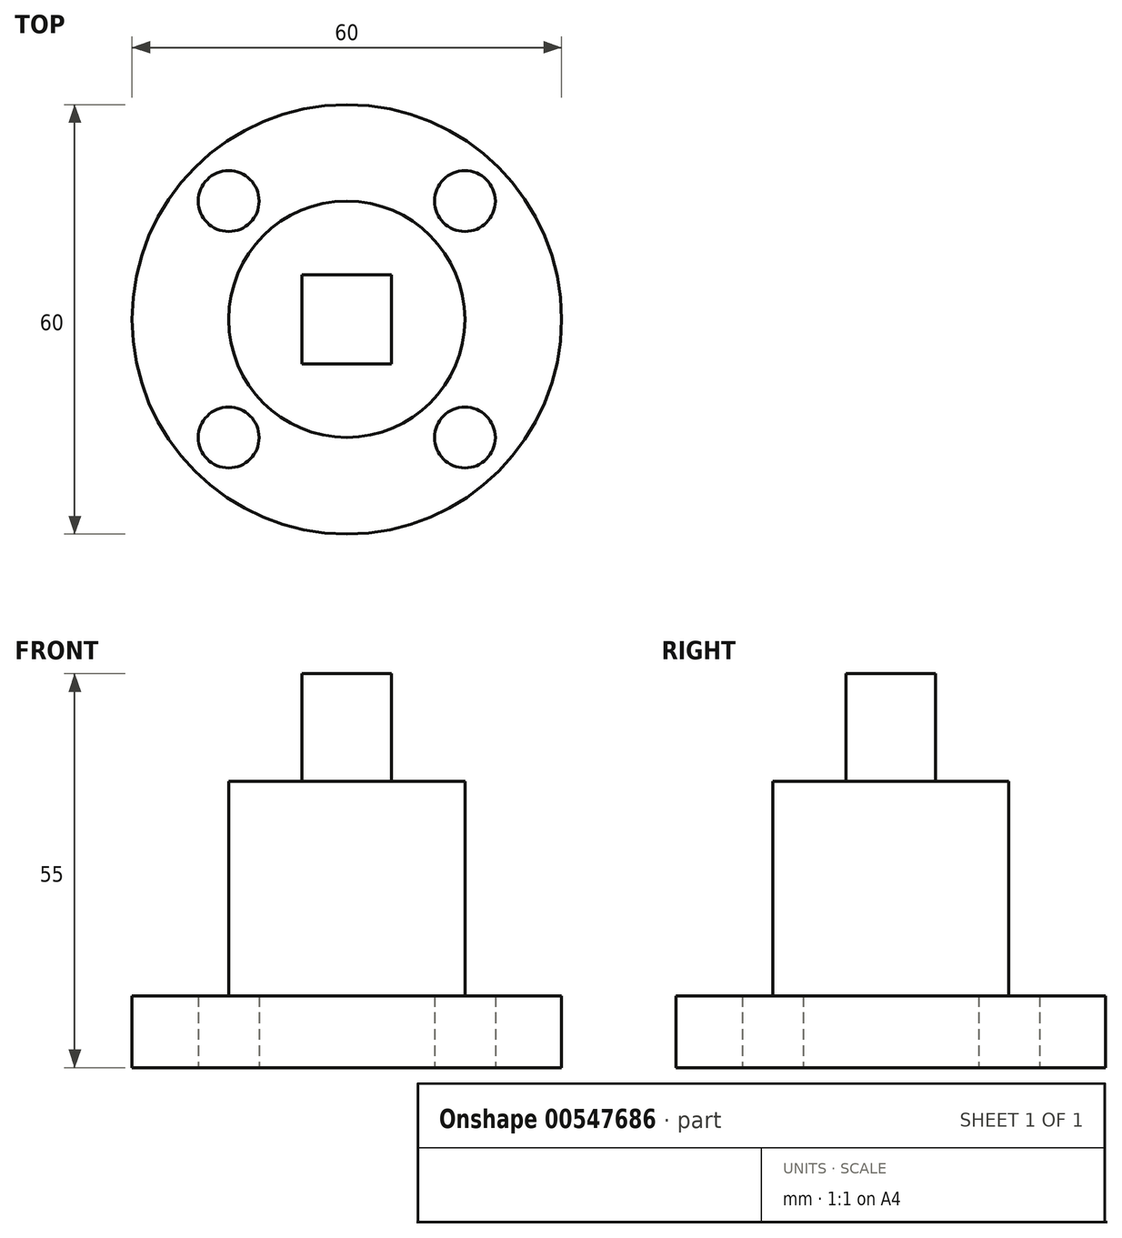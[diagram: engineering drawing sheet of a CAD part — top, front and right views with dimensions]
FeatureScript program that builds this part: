
annotation { "Feature Type Name" : "Feature", "Feature Type Description" : "" }
export const myFeature = defineFeature(function(context is Context, id is Id, definition is map)
    precondition{}
    {
        {
            var Q0;
            Q0=qCreatedBy(makeId("Top.planeOp"),FACE);
            var sketch = newSketch(context, id + "F0", { "sketchPlane" : qUnion([Q0])});
            skCircle(sketch, "E0", {"center": v(-16.5, 16.51) * mm, "radius": 4.25 * mm});
            skCircle(sketch, "E1", {"center": v(0, 0) * mm, "radius": 30 * mm});
            skCircle(sketch, "E2.MirrorC", {"center": v(16.5, 16.51) * mm, "radius": 4.25 * mm});
            skCircle(sketch, "E3.MirrorC", {"center": v(-16.5, -16.51) * mm, "radius": 4.25 * mm});
            skCircle(sketch, "E4.MirrorC", {"center": v(16.5, -16.51) * mm, "radius": 4.25 * mm});
            skSolve(sketch);
        }
        {
            var Q0;
            Q0 = qSketchRegion(id + "F0", true);
            extrude(context, id + "F1", {"entities" : qUnion([Q0]), "depth" : 10 * mm, "offsetDistance" : 25.4 * mm});
        }
        {
            var Q0;
            Q0=makeQuery(id+"F1.opExtrude","CAP_FACE",FACE,{"disambiguationData":[OSD([sQuery(id+"F0.wireOp",EDGE,"E1"),sQuery(id+"F0.wireOp",EDGE,"E2.MirrorC"),sQuery(id+"F0.wireOp",EDGE,"E3.MirrorC"),sQuery(id+"F0.wireOp",EDGE,"E0"),sQuery(id+"F0.wireOp",EDGE,"E4.MirrorC")])],"isStart":false});
            var sketch = newSketch(context, id + "F2", { "sketchPlane" : qUnion([Q0])});
            skCircle(sketch, "E5", {"center": v(0, 0) * mm, "radius": 16.5 * mm});
            skSolve(sketch);
        }
        {
            var Q0;
            Q0 = qSketchRegion(id + "F2", true);
            extrude(context, id + "F3", {"entities" : qUnion([Q0]), "operationType" : NewBodyOperationType.ADD, "depth" : 30 * mm, "offsetDistance" : 25.4 * mm});
        }
        {
            var Q0;
            Q0=makeQuery(id+"F3.opExtrude","CAP_FACE",FACE,{"disambiguationData":[OSD([sQuery(id+"F2.wireOp",EDGE,"E5")])],"isStart":false});
            var sketch = newSketch(context, id + "F4", { "sketchPlane" : qUnion([Q0])});
            skLineSegment(sketch, "E6.bottom", {"start": v(6.25, -6.25) * mm, "end": v(-6.25, -6.25) * mm});
            skLineSegment(sketch, "E6.top", {"start": v(6.25, 6.25) * mm, "end": v(-6.25, 6.25) * mm});
            skLineSegment(sketch, "E6.left", {"start": v(6.25, -6.25) * mm, "end": v(6.25, 6.25) * mm});
            skLineSegment(sketch, "E6.right", {"start": v(-6.25, -6.25) * mm, "end": v(-6.25, 6.25) * mm});
            skPoint(sketch, "E6.middle", {"position": v(0, 0) * mm});
            skSolve(sketch);
        }
        {
            var Q0;
            Q0 = qSketchRegion(id + "F4", true);
            extrude(context, id + "F5", {"entities" : qUnion([Q0]), "operationType" : NewBodyOperationType.ADD, "depth" : 15 * mm, "offsetDistance" : 25.4 * mm});
        }
    });
